# Revit family: ВШК_Eng
name_source: partatom
category: Mechanical Equipment
units: mm (PartAtom-declared; Revit-internal decimal feet)

## family parameters
Always vertical = Yes
Classification = None
Cut with Voids When Loaded = No
Part Type = Normal
Room Calculation Point = No
Round Connector Dimension = Use Diameter
Shared = No
Work Plane-Based = No

## types (17) — shared parameters
00_20_Manufacturer = Vents
00_20_Name = Sound-insulated kitchen fan
Casing Material = Steel, galvanized
Frequency = 50 Hz
Grid Material = Mesh, steel, painted, RAL5007
Maintenance zone material = <By Category>
Manufacturer = Vents
The right outlet is closed = Yes
URL = https://ventilation-system.com
zero-valued in all types: Default Elevation

## per-type parameters (varying)
- VSK 315 2D: 00_20_Type=VSK 315 2D; Alfa=0.00°; Amperage=2 A; B=500 mm; B1=270 mm; B2=150 mm; Diameter=315 mm; Dy=315 mm; H=500 mm; H1=250 mm; H2=105 mm  [stored 0.344488 ft]; H3=400 mm; Height=540 mm; L=500 mm; L1=300 mm; Le=250 mm; Length=500 mm; Load Classification=HVAC; Maximum Air Flow=1240.0 L/s; Motor=Motor : Motor_1.1 kW; Number of Fase=3; Power=1100 W; R=225 mm; R1=131 mm; R2=111 mm; R3=150 mm; The left outlet is closed=No; The upward discharge is closed=Yes; Voltage=400 V; Weight=41 kg; Width=550 mm; t=10 mm  [stored 0.0328084 ft]; t1=89 mm; t2=20 mm  [stored 0.0656168 ft]; t3=159 mm  [stored 0.521654 ft]
- VSK 800 6D: 00_20_Type=VSK 800 6D; Alfa=0.00°; Amperage=9 A; B=1175 mm; B1=635 mm; B2=488 mm; Diameter=800 mm; Dy=800 mm; H=1175 mm; H1=588 mm; H2=413 mm; H3=1075 mm; Height=1215 mm; L=1175 mm; L1=350 mm; Le=588 mm; Length=1175 mm; Load Classification=HVAC; Maximum Air Flow=6070.0 L/s; Motor=Motor : Motor_4 kW; Number of Fase=3; Power=4000 W; R=529 mm; R1=308 mm; R2=261 mm; R3=353 mm; The left outlet is closed=No; The upward discharge is closed=Yes; Voltage=400 V; Weight=275 kg; Width=1225 mm; t=24 mm  [stored 0.0787402 ft]; t1=210 mm; t2=47 mm  [stored 0.154199 ft]; t3=361 mm
- VSK 315 2E: 00_20_Type=VSK 315 2Е; Alfa=0.00°; Amperage=8 A; B=500 mm; B1=270 mm; B2=150 mm; Diameter=315 mm; Dy=315 mm; H=500 mm; H1=250 mm; H2=105 mm  [stored 0.344488 ft]; H3=400 mm; Height=540 mm; L=500 mm; L1=300 mm; Le=250 mm; Length=500 mm; Load Classification=HVAC; Maximum Air Flow=1240.0 L/s; Motor=Motor : Motor_1.1 kW; Number of Fase=1; Power=1100 W; R=225 mm; R1=131 mm; R2=111 mm; R3=150 mm; The left outlet is closed=No; The upward discharge is closed=Yes; Voltage=230 V; Weight=40.2 kg; Width=550 mm; t=10 mm  [stored 0.0328084 ft]; t1=89 mm; t2=20 mm  [stored 0.0656168 ft]; t3=159 mm  [stored 0.521654 ft]
- VSK 315 4D: 00_20_Type=VSK 315 4D; Alfa=0.00°; Amperage=1 A; B=500 mm; B1=270 mm; B2=150 mm; Diameter=315 mm; Dy=315 mm; H=500 mm; H1=250 mm; H2=145 mm  [stored 0.475722 ft]; H3=400 mm; Height=540 mm; L=500 mm; L1=210 mm; Le=250 mm; Length=500 mm; Load Classification=HVAC; Maximum Air Flow=530.0 L/s; Motor=Motor : Motor_0.25 kW; Number of Fase=3; Power=250 W; R=225 mm; R1=131 mm; R2=111 mm; R3=150 mm; The left outlet is closed=No; The upward discharge is closed=Yes; Voltage=400 V; Weight=37.2 kg; Width=550 mm; t=10 mm  [stored 0.0328084 ft]; t1=89 mm; t2=20 mm  [stored 0.0656168 ft]; t3=159 mm  [stored 0.521654 ft]
- VSK 315 4E: 00_20_Type=VSK 315 4Е; Alfa=0.00°; Amperage=2 A; B=500 mm; B1=270 mm; B2=150 mm; Diameter=315 mm; Dy=315 mm; H=500 mm; H1=250 mm; H2=145 mm  [stored 0.475722 ft]; H3=400 mm; Height=540 mm; L=500 mm; L1=210 mm; Le=250 mm; Length=500 mm; Load Classification=HVAC; Maximum Air Flow=530.0 L/s; Motor=Motor : Motor_0.25 kW; Number of Fase=1; Power=250 W; R=225 mm; R1=131 mm; R2=111 mm; R3=150 mm; The left outlet is closed=No; The upward discharge is closed=Yes; Voltage=230 V; Weight=37.2 kg; Width=550 mm; t=10 mm  [stored 0.0328084 ft]; t1=89 mm; t2=20 mm  [stored 0.0656168 ft]; t3=159 mm  [stored 0.521654 ft]
- VSK 355 4D: 00_20_Type=VSK 355 4D; Alfa=0.00°; Amperage=1 A; B=600 mm; B1=324 mm; B2=200 mm; Diameter=355 mm; Dy=355 mm; H=600 mm; H1=300 mm; H2=195 mm; H3=500 mm; Height=640 mm; L=600 mm; L1=210 mm; Le=300 mm; Length=600 mm; Load Classification=HVAC; Maximum Air Flow=890.0 L/s; Motor=Motor : Motor_0.37 kW; Number of Fase=3; Power=370 W; R=270 mm; R1=158 mm; R2=133 mm; R3=180 mm  [stored 0.590551 ft]; The left outlet is closed=No; The upward discharge is closed=Yes; Voltage=400 V; Weight=48.1 kg; Width=650 mm; t=12 mm  [stored 0.0393701 ft]; t1=107 mm; t2=24 mm  [stored 0.0787402 ft]; t3=189 mm
- VSK 355 4E: 00_20_Type=VSK 355 4Е; Alfa=0.00°; Amperage=3 A; B=600 mm; B1=324 mm; B2=200 mm; Diameter=355 mm; Dy=355 mm; H=600 mm; H1=300 mm; H2=195 mm; H3=500 mm; Height=640 mm; L=600 mm; L1=210 mm; Le=300 mm; Length=600 mm; Load Classification=HVAC; Maximum Air Flow=890.0 L/s; Motor=Motor : Motor_0.37 kW; Number of Fase=1; Power=370 W; R=270 mm; R1=158 mm; R2=133 mm; R3=180 mm  [stored 0.590551 ft]; The left outlet is closed=No; The upward discharge is closed=Yes; Voltage=230 V; Weight=47.4 kg; Width=650 mm; t=12 mm  [stored 0.0393701 ft]; t1=107 mm; t2=24 mm  [stored 0.0787402 ft]; t3=189 mm
- VSK 400 4E: 00_20_Type=VSK 400 4Е; Alfa=0.00°; Amperage=4 A; B=670 mm; B1=362 mm; B2=235 mm; Diameter=400 mm; Dy=400 mm; H=670 mm; H1=335 mm; H2=230 mm; H3=570 mm; Height=710 mm; L=670 mm; L1=210 mm; Le=335 mm; Length=670 mm; Load Classification=HVAC; Maximum Air Flow=1260.0 L/s; Motor=Motor : Motor_0.55 kW; Number of Fase=1; Power=550 W; R=302 mm; R1=176 mm; R2=149 mm; R3=201 mm; The left outlet is closed=No; The upward discharge is closed=Yes; Voltage=230 V; Weight=60.3 kg; Width=720 mm; t=13 mm; t1=120 mm  [stored 0.393701 ft]; t2=27 mm; t3=210 mm
- VSK 400 4D: 00_20_Type=VSK 400 4D; Alfa=0.00°; Amperage=2 A; B=670 mm; B1=362 mm; B2=235 mm; Diameter=400 mm; Dy=400 mm; H=670 mm; H1=335 mm; H2=230 mm; H3=570 mm; Height=710 mm; L=670 mm; L1=210 mm; Le=335 mm; Length=670 mm; Load Classification=73.3; Maximum Air Flow=1260.0 L/s; Motor=Motor : Motor_0.55 kW; Number of Fase=3; Power=550 W; R=302 mm; R1=176 mm; R2=149 mm; R3=201 mm; The left outlet is closed=No; The upward discharge is closed=Yes; Voltage=400 V; Weight=73.3 kg; Width=720 mm; t=13 mm; t1=120 mm  [stored 0.393701 ft]; t2=27 mm; t3=210 mm
- VSK 450 4E: 00_20_Type=VSK 450 4Е; Alfa=0.00°; Amperage=6 A; B=700 mm; B1=378 mm; B2=250 mm; Diameter=450 mm; Dy=450 mm; H=700 mm; H1=350 mm; H2=245 mm; H3=600 mm; Height=740 mm; L=700 mm; L1=210 mm; Le=350 mm; Length=700 mm; Load Classification=HVAC; Maximum Air Flow=1650.0 L/s; Motor=Motor : Motor_0.75 kW; Number of Fase=1; Power=750 W; R=315 mm; R1=184 mm; R2=156 mm; R3=210 mm; The left outlet is closed=No; The upward discharge is closed=Yes; Voltage=230 V; Weight=71.8 kg; Width=750 mm; t=14 mm  [stored 0.0459318 ft]; t1=125 mm  [stored 0.410105 ft]; t2=28 mm  [stored 0.0918635 ft]; t3=219 mm
- VSK 450 4D: 00_20_Type=VSK 450 4D; Alfa=0.00°; Amperage=2 A; B=700 mm; B1=378 mm; B2=250 mm; Diameter=450 mm; Dy=450 mm; H=700 mm; H1=350 mm; H2=245 mm; H3=600 mm; Height=740 mm; L=700 mm; L1=210 mm; Le=350 mm; Length=700 mm; Load Classification=HVAC; Maximum Air Flow=1650.0 L/s; Motor=Motor : Motor_0.75 kW; Number of Fase=3; Power=750 W; R=315 mm; R1=184 mm; R2=156 mm; R3=210 mm; The left outlet is closed=No; The upward discharge is closed=Yes; Voltage=400 V; Weight=73.3 kg; Width=750 mm; t=14 mm  [stored 0.0459318 ft]; t1=125 mm  [stored 0.410105 ft]; t2=28 mm  [stored 0.0918635 ft]; t3=219 mm
- VSK 500 4D: 00_20_Type=VSK 500 4D; Alfa=0.00°; Amperage=3 A; B=820 mm; B1=443 mm; B2=310 mm; Diameter=500 mm; Dy=500 mm; H=820 mm; H1=410 mm; H2=260 mm; H3=720 mm; Height=860 mm; L=820 mm; L1=300 mm; Le=410 mm; Length=820 mm; Load Classification=HVAC; Maximum Air Flow=2530.0 L/s; Motor=Motor : Motor_1.5 kW; Number of Fase=3; Power=1500 W; R=369 mm; R1=215 mm; R2=182 mm; R3=246 mm; The left outlet is closed=No; The upward discharge is closed=Yes; Voltage=400 V; Weight=101.8 kg; Width=870 mm; t=16 mm  [stored 0.0524934 ft]; t1=146 mm; t2=33 mm; t3=255 mm
- VSK 500 4E: 00_20_Type=VSK 500 4Е; Alfa=90.00°; Amperage=11 A; B=820 mm; B1=443 mm; B2=310 mm; Diameter=500 mm; Dy=500 mm; H=820 mm; H1=410 mm; H2=260 mm; H3=720 mm; Height=860 mm; L=820 mm; L1=300 mm; Le=410 mm; Length=820 mm; Load Classification=HVAC; Maximum Air Flow=2530.0 L/s; Motor=Motor : Motor_1.5 kW; Number of Fase=1; Power=1500 W; R=369 mm; R1=215 mm; R2=182 mm; R3=246 mm; The left outlet is closed=Yes; The upward discharge is closed=No; Voltage=230 V; Weight=96.3 kg; Width=870 mm; t=16 mm  [stored 0.0524934 ft]; t1=146 mm; t2=33 mm; t3=255 mm
- VSK 560 4D: 00_20_Type=VSK 560 4D; Alfa=0.00°; Amperage=6 A; B=900 mm; B1=486 mm; B2=350 mm; Diameter=560 mm; Dy=560 mm; H=900 mm; H1=450 mm; H2=295 mm; H3=800 mm; Height=940 mm; L=900 mm; L1=300 mm; Le=450 mm; Length=900 mm; Load Classification=HVAC; Maximum Air Flow=3540.0 L/s; Motor=Motor : Motor_3 kW; Number of Fase=3; Power=3000 W; R=405 mm; R1=236 mm; R2=200 mm; R3=270 mm; The left outlet is closed=No; The upward discharge is closed=Yes; Voltage=400 V; Weight=130.3 kg; Width=950 mm; t=18 mm  [stored 0.0590551 ft]; t1=161 mm; t2=36 mm  [stored 0.11811 ft]; t3=279 mm
- VSK 630 4D: 00_20_Type=VSK 630 4D; Alfa=0.00°; Amperage=8 A; B=1000 mm; B1=540 mm; B2=400 mm; Diameter=630 mm; Dy=630 mm; H=1000 mm; H1=500 mm; H2=325 mm; H3=900 mm; Height=1040 mm; L=1000 mm; L1=350 mm; Le=500 mm; Length=1000 mm; Load Classification=HVAC; Maximum Air Flow=4800.0 L/s; Motor=Motor : Motor_4 kW; Number of Fase=3; Power=4000 W; R=450 mm; R1=263 mm; R2=222 mm; R3=300 mm; The left outlet is closed=No; The upward discharge is closed=Yes; Voltage=400 V; Weight=173.8 kg; Width=1050 mm; t=20 mm  [stored 0.0656168 ft]; t1=179 mm; t2=40 mm  [stored 0.131234 ft]; t3=309 mm
- VSK 710 6D: 00_20_Type=VSK 710 6D; Alfa=0.00°; Amperage=5 A; B=1075 mm; B1=581 mm; B2=438 mm; Diameter=700 mm; Dy=700 mm; H=1075 mm; H1=538 mm; H2=383 mm; H3=975 mm; Height=1115 mm; L=1075 mm; L1=350 mm; Le=538 mm; Length=1075 mm; Load Classification=HVAC; Maximum Air Flow=4555.0 L/s; Motor=Motor : Motor_2.2 kW; Number of Fase=3; Power=2200 W; R=484 mm; R1=282 mm; R2=239 mm; R3=323 mm; The left outlet is closed=No; The upward discharge is closed=Yes; Voltage=400 V; Weight=210 kg; Width=1125 mm; t=22 mm  [stored 0.0721785 ft]; t1=192 mm; t2=43 mm  [stored 0.141076 ft]; t3=331 mm
- VSK 710 4D: 00_20_Type=VSK 710 4D; Alfa=0.00°; Amperage=16 A; B=1075 mm; B1=581 mm; B2=438 mm; Diameter=700 mm; Dy=700 mm; H=1075 mm; H1=538 mm; H2=363 mm; H3=975 mm; Height=1115 mm; L=1075 mm; L1=350 mm; Le=538 mm; Length=1075 mm; Load Classification=HVAC; Maximum Air Flow=7080.0 L/s; Motor=Motor : Motor_4 kW; Number of Fase=3; Power=7500 W; R=484 mm; R1=282 mm; R2=239 mm; R3=323 mm; The left outlet is closed=No; The upward discharge is closed=Yes; Voltage=400 V; Weight=240 kg; Width=1125 mm; t=22 mm  [stored 0.0721785 ft]; t1=192 mm; t2=43 mm  [stored 0.141076 ft]; t3=331 mm

note: [stored X ft] marks values corroborated as IEEE doubles in the binary element streams (Revit-internal decimal feet)
